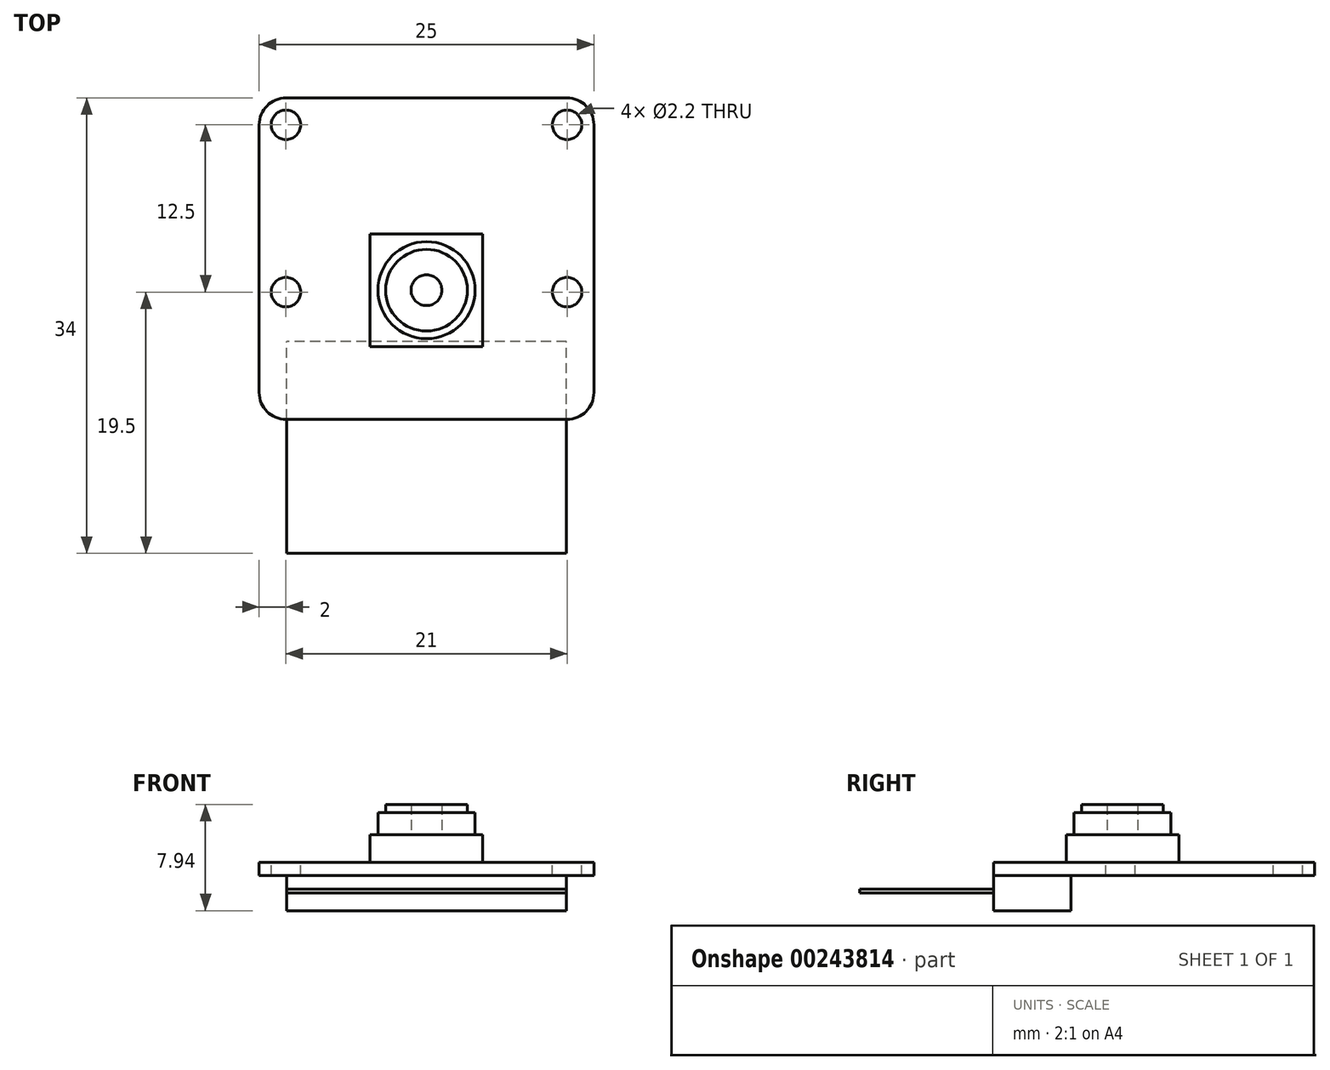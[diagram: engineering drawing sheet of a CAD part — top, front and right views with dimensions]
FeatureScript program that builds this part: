
annotation { "Feature Type Name" : "Feature", "Feature Type Description" : "" }
export const myFeature = defineFeature(function(context is Context, id is Id, definition is map)
    precondition{}
    {
        {
            var Q0;
            Q0=qCreatedBy(makeId("Top.planeOp"),FACE);
            var sketch = newSketch(context, id + "F0", { "sketchPlane" : qUnion([Q0])});
            skLineSegment(sketch, "E0.bottom", {"start": v(10.5, 12) * mm, "end": v(-10.5, 12) * mm});
            skLineSegment(sketch, "E0.top", {"start": v(10.5, -12) * mm, "end": v(-10.5, -12) * mm});
            skLineSegment(sketch, "E0.left", {"start": v(12.5, 10) * mm, "end": v(12.5, -10) * mm});
            skLineSegment(sketch, "E0.right", {"start": v(-12.5, 10) * mm, "end": v(-12.5, -10) * mm});
            skPoint(sketch, "E0.middle", {"position": v(0, 0) * mm});
            skPoint(sketch, "E1.visualSharp", {"position": v(-12.5, 12) * mm});
            skArc(sketch, "E1.filletArc", {"start": v(-10.5, 12) * mm, "mid": v(-11.91, 11.41) * mm, "end": v(-12.5, 10) * mm});
            skPoint(sketch, "E2.visualSharp", {"position": v(12.5, 12) * mm});
            skArc(sketch, "E2.filletArc", {"start": v(12.5, 10) * mm, "mid": v(11.91, 11.41) * mm, "end": v(10.5, 12) * mm});
            skPoint(sketch, "E3.visualSharp", {"position": v(12.5, -12) * mm});
            skArc(sketch, "E3.filletArc", {"start": v(10.5, -12) * mm, "mid": v(11.91, -11.41) * mm, "end": v(12.5, -10) * mm});
            skPoint(sketch, "E4.visualSharp", {"position": v(-12.5, -12) * mm});
            skArc(sketch, "E4.filletArc", {"start": v(-12.5, -10) * mm, "mid": v(-11.91, -11.41) * mm, "end": v(-10.5, -12) * mm});
            skSolve(sketch);
        }
        {
            var Q0;
            Q0=makeQuery(id+"F0.imprint","IMPRINT",FACE,{"disambiguationData":[TD([[makeQuery(id+"F0.imprint","IMPRINT",EDGE,{"derivedFrom":sQuery(id+"F0.wireOp",EDGE,"E0.bottom")}),1.0]])]});
            extrude(context, id + "F1", {"entities" : qUnion([Q0]), "oppositeDirection" : true, "depth" : 1 * mm});
        }
        {
            var Q0;
            Q0=makeQuery(id+"F1.opExtrude","CAP_FACE",FACE,{"disambiguationData":[OSD([sQuery(id+"F0.wireOp",EDGE,"E0.bottom"),sQuery(id+"F0.wireOp",EDGE,"E0.top"),sQuery(id+"F0.wireOp",EDGE,"E0.left"),sQuery(id+"F0.wireOp",EDGE,"E0.right"),sQuery(id+"F0.wireOp",EDGE,"E1.filletArc"),sQuery(id+"F0.wireOp",EDGE,"E2.filletArc"),sQuery(id+"F0.wireOp",EDGE,"E3.filletArc"),sQuery(id+"F0.wireOp",EDGE,"E4.filletArc")])],"isStart":true});
            var sketch = newSketch(context, id + "F2", { "sketchPlane" : qUnion([Q0])});
            skCircle(sketch, "E5", {"center": v(-10.5, 10) * mm, "radius": 1.1 * mm});
            skCircle(sketch, "E6", {"center": v(-10.5, -2.5) * mm, "radius": 1.1 * mm});
            skCircle(sketch, "E7.MirrorC", {"center": v(10.5, -2.5) * mm, "radius": 1.1 * mm});
            skCircle(sketch, "E8.MirrorC", {"center": v(10.5, 10) * mm, "radius": 1.1 * mm});
            skSolve(sketch);
        }
        {
            var Q0;
            Q0=qSketchRegion(id+"F2",true);
            extrude(context, id + "F3", {"entities" : qUnion([Q0]), "operationType" : NewBodyOperationType.REMOVE, "endBound" : BoundingType.UP_TO_NEXT, "oppositeDirection" : true, "depth" : 25 * mm});
        }
        {
            var Q0;
            Q0=makeQuery(id+"F1.opExtrude","CAP_FACE",FACE,{"disambiguationData":[OSD([sQuery(id+"F0.wireOp",EDGE,"E0.bottom"),sQuery(id+"F0.wireOp",EDGE,"E0.top"),sQuery(id+"F0.wireOp",EDGE,"E0.left"),sQuery(id+"F0.wireOp",EDGE,"E0.right"),sQuery(id+"F0.wireOp",EDGE,"E1.filletArc"),sQuery(id+"F0.wireOp",EDGE,"E2.filletArc"),sQuery(id+"F0.wireOp",EDGE,"E3.filletArc"),sQuery(id+"F0.wireOp",EDGE,"E4.filletArc")])],"isStart":true});
            var sketch = newSketch(context, id + "F4", { "sketchPlane" : qUnion([Q0])});
            skLineSegment(sketch, "E9.bottom", {"start": v(4.2, 1.85) * mm, "end": v(-4.2, 1.85) * mm});
            skLineSegment(sketch, "E9.top", {"start": v(4.2, -6.56) * mm, "end": v(-4.2, -6.56) * mm});
            skLineSegment(sketch, "E9.left", {"start": v(4.2, 1.85) * mm, "end": v(4.2, -6.56) * mm});
            skLineSegment(sketch, "E9.right", {"start": v(-4.2, 1.85) * mm, "end": v(-4.2, -6.56) * mm});
            skPoint(sketch, "E9.middle", {"position": v(0, -2.36) * mm});
            skSolve(sketch);
        }
        {
            var Q0;
            Q0=qSketchRegion(id+"F4",true);
            extrude(context, id + "F5", {"entities" : qUnion([Q0]), "depth" : 2.05 * mm});
        }
        {
            var Q0;
            Q0=makeQuery(id+"F5.opExtrude","CAP_FACE",FACE,{"disambiguationData":[OSD([sQuery(id+"F4.wireOp",EDGE,"E9.bottom"),sQuery(id+"F4.wireOp",EDGE,"E9.top"),sQuery(id+"F4.wireOp",EDGE,"E9.left"),sQuery(id+"F4.wireOp",EDGE,"E9.right")])],"isStart":false});
            var sketch = newSketch(context, id + "F6", { "sketchPlane" : qUnion([Q0])});
            skCircle(sketch, "E10", {"center": v(0, -2.36) * mm, "radius": 3.62 * mm});
            skLineSegment(sketch, "E11", {"start": v(0, 1.85) * mm, "end": v(0, -6.56) * mm, "construction": true});
            skLineSegment(sketch, "E12", {"start": v(-4.2, -2.36) * mm, "end": v(4.2, -2.36) * mm, "construction": true});
            skCircle(sketch, "E13", {"center": v(0, -2.36) * mm, "radius": 3.05 * mm});
            skCircle(sketch, "E14", {"center": v(0, -2.36) * mm, "radius": 1.15 * mm});
            skSolve(sketch);
        }
        {
            var Q0;
            Q0=qSketchRegion(id+"F6",true);
            var Q1;
            Q1=makeQuery(id+"F6.imprint","IMPRINT",FACE,{"disambiguationData":[TD([[makeQuery(id+"F6.imprint","IMPRINT",EDGE,{"derivedFrom":sQuery(id+"F6.wireOp",EDGE,"E13")}),1.0]])]});
            var Q2;
            Q2=makeQuery(id+"F6.imprint","IMPRINT",FACE,{"disambiguationData":[TD([[makeQuery(id+"F6.imprint","IMPRINT",EDGE,{"derivedFrom":sQuery(id+"F6.wireOp",EDGE,"E14")}),1.0]])]});
            extrude(context, id + "F7", {"entities" : qUnion([Q0, Q1, Q2]), "operationType" : NewBodyOperationType.ADD, "depth" : 1.65 * mm});
        }
        {
            var Q0;
            Q0=makeQuery(id+"F6.imprint","IMPRINT",FACE,{"disambiguationData":[TD([[makeQuery(id+"F6.imprint","IMPRINT",EDGE,{"derivedFrom":sQuery(id+"F6.wireOp",EDGE,"E13")}),1.0]])]});
            var Q1;
            Q1=makeQuery(id+"F6.imprint","IMPRINT",FACE,{"disambiguationData":[TD([[makeQuery(id+"F6.imprint","IMPRINT",EDGE,{"derivedFrom":sQuery(id+"F6.wireOp",EDGE,"E14")}),1.0]])]});
            extrude(context, id + "F8", {"entities" : qUnion([Q0, Q1]), "operationType" : NewBodyOperationType.ADD, "depth" : 2.25 * mm});
        }
        {
            var Q0;
            Q0=makeQuery(id+"F6.imprint","IMPRINT",FACE,{"disambiguationData":[TD([[makeQuery(id+"F6.imprint","IMPRINT",EDGE,{"derivedFrom":sQuery(id+"F6.wireOp",EDGE,"E14")}),1.0]])]});
            extrude(context, id + "F9", {"entities" : qUnion([Q0]), "depth" : 2.27 * mm});
        }
        {
            var Q0;
            Q0=makeQuery(id+"F1.opExtrude","CAP_FACE",FACE,{"disambiguationData":[OSD([sQuery(id+"F0.wireOp",EDGE,"E0.bottom"),sQuery(id+"F0.wireOp",EDGE,"E0.top"),sQuery(id+"F0.wireOp",EDGE,"E0.left"),sQuery(id+"F0.wireOp",EDGE,"E0.right"),sQuery(id+"F0.wireOp",EDGE,"E1.filletArc"),sQuery(id+"F0.wireOp",EDGE,"E2.filletArc"),sQuery(id+"F0.wireOp",EDGE,"E3.filletArc"),sQuery(id+"F0.wireOp",EDGE,"E4.filletArc")])],"isStart":false});
            var sketch = newSketch(context, id + "F10", { "sketchPlane" : qUnion([Q0])});
            skLineSegment(sketch, "E15.bottom", {"start": v(10.45, 12) * mm, "end": v(-10.45, 12) * mm});
            skLineSegment(sketch, "E15.top", {"start": v(10.45, 6.2) * mm, "end": v(-10.45, 6.2) * mm});
            skLineSegment(sketch, "E15.left", {"start": v(10.45, 12) * mm, "end": v(10.45, 6.2) * mm});
            skLineSegment(sketch, "E15.right", {"start": v(-10.45, 12) * mm, "end": v(-10.45, 6.2) * mm});
            skPoint(sketch, "E15.middle", {"position": v(0, 9.1) * mm});
            skSolve(sketch);
        }
        {
            var Q0;
            Q0=qSketchRegion(id+"F10",true);
            extrude(context, id + "F11", {"entities" : qUnion([Q0]), "depth" : 2.62 * mm});
        }
        {
            var Q0;
            Q0=makeQuery(id+"F11.boolean.opBoolean","MERGE",FACE,{"derivedFrom":[makeQuery(id+"F1.opExtrude","SWEPT_FACE",FACE,{"disambiguationData":[OSD([sQuery(id+"F0.wireOp",EDGE,"E0.top")])]}),makeQuery(id+"F11.opExtrude","SWEPT_FACE",FACE,{"disambiguationData":[OSD([sQuery(id+"F10.wireOp",EDGE,"E15.bottom")])]})]});
            var sketch = newSketch(context, id + "F12", { "sketchPlane" : qUnion([Q0])});
            skLineSegment(sketch, "E16.bottom", {"start": v(-10.45, -2) * mm, "end": v(10.45, -2) * mm});
            skLineSegment(sketch, "E16.top", {"start": v(-10.45, -2.31) * mm, "end": v(10.45, -2.31) * mm});
            skLineSegment(sketch, "E16.left", {"start": v(-10.45, -2) * mm, "end": v(-10.45, -2.31) * mm});
            skLineSegment(sketch, "E16.right", {"start": v(10.45, -2) * mm, "end": v(10.45, -2.31) * mm});
            skSolve(sketch);
        }
        {
            var Q0;
            Q0=qSketchRegion(id+"F12",true);
            extrude(context, id + "F13", {"entities" : qUnion([Q0]), "depth" : 10 * mm});
        }
    });
